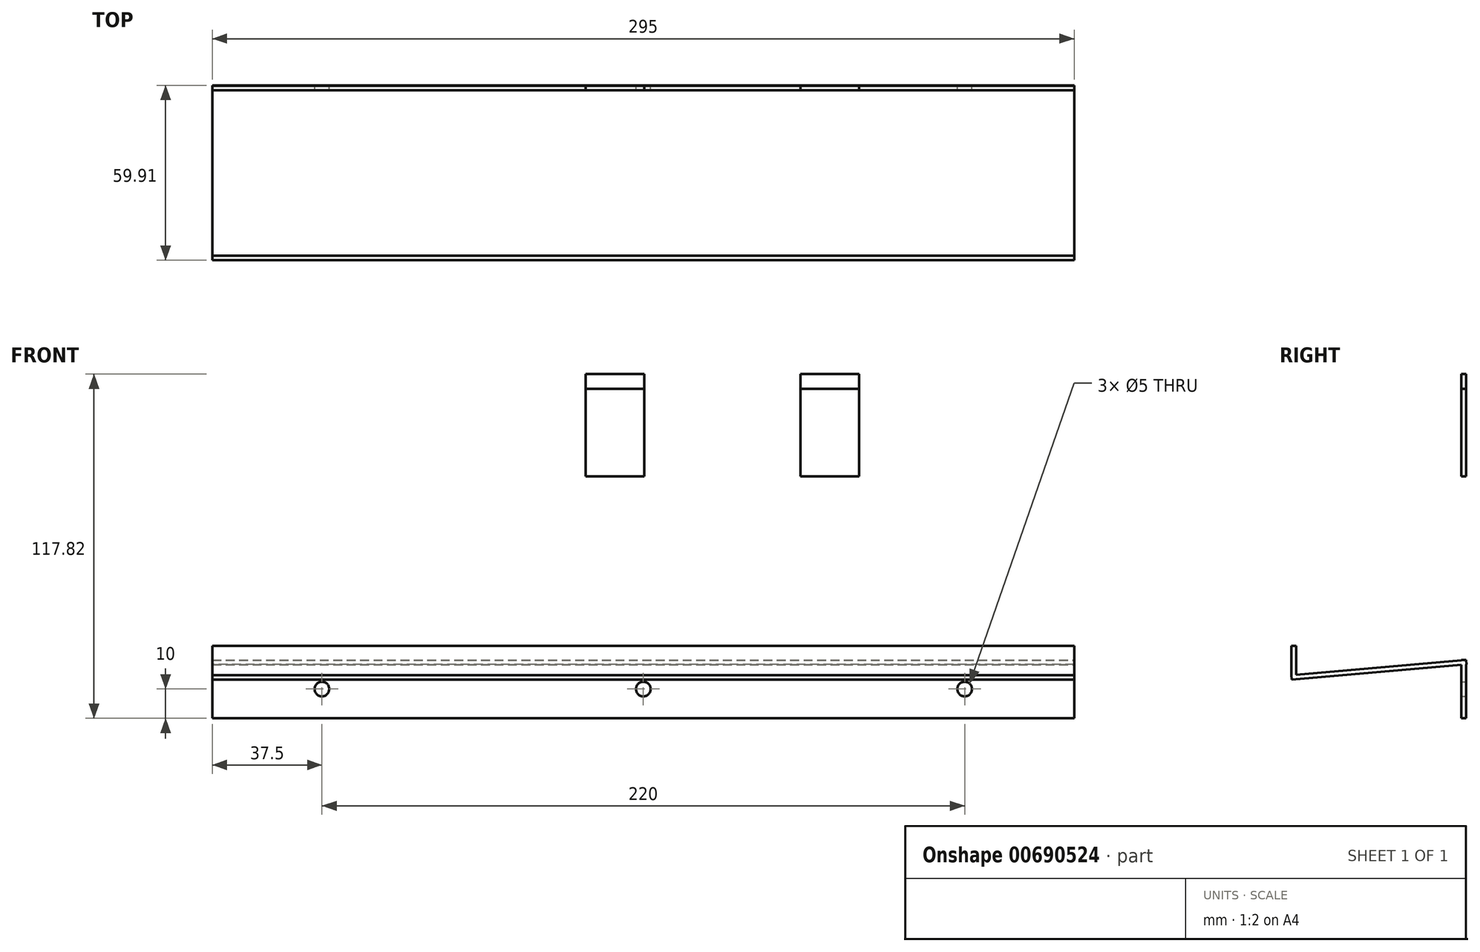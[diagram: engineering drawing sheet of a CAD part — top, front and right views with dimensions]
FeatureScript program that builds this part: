
annotation { "Feature Type Name" : "Feature", "Feature Type Description" : "" }
export const myFeature = defineFeature(function(context is Context, id is Id, definition is map)
    precondition{}
    {
        {
            var Q0;
            Q0=qCreatedBy(makeId("Front.planeOp"),FACE);
            var sketch = newSketch(context, id + "F0", { "sketchPlane" : qUnion([Q0])});
            skLineSegment(sketch, "E0.bottom", {"start": v(0, 0) * mm, "end": v(295, 0) * mm});
            skLineSegment(sketch, "E0.top", {"start": v(0, 20) * mm, "end": v(295, 20) * mm});
            skLineSegment(sketch, "E0.left", {"start": v(0, 0) * mm, "end": v(0, 20) * mm});
            skLineSegment(sketch, "E0.right", {"start": v(295, 0) * mm, "end": v(295, 20) * mm});
            skCircle(sketch, "E1", {"center": v(37.5, 10) * mm, "radius": 2.5 * mm});
            skCircle(sketch, "E2", {"center": v(147.5, 10) * mm, "radius": 2.5 * mm});
            skCircle(sketch, "E3", {"center": v(257.5, 10) * mm, "radius": 2.5 * mm});
            skPoint(sketch, "E4", {"position": v(295, 10) * mm});
            skPoint(sketch, "E5", {"position": v(147.5, 20) * mm});
            skLineSegment(sketch, "E6.bottom", {"start": v(20, 20) * mm, "end": v(275, 20) * mm});
            skLineSegment(sketch, "E6.top", {"start": v(20, 0) * mm, "end": v(275, 0) * mm});
            skLineSegment(sketch, "E6.left", {"start": v(20, 20) * mm, "end": v(20, 0) * mm});
            skLineSegment(sketch, "E6.right", {"start": v(275, 20) * mm, "end": v(275, 0) * mm});
            skSolve(sketch);
        }
        {
            var Q0;
            Q0=sQuery(id+"F0.wireOp",EDGE,"E0.top");
            cPlane(context, id + "F1", {"entities" : qUnion([Q0]), "cplaneType" : CPlaneType.LINE_ANGLE, "offset" : 25 * mm, "angle" : 85 * degree, "oppositeDirection" : true, "width" : 150 * mm, "height" : 150 * mm});
        }
        {
            var Q0;
            Q0=qCreatedBy(id+"F1.planeOp",FACE);
            var sketch = newSketch(context, id + "F2", { "sketchPlane" : qUnion([Q0])});
            skLineSegment(sketch, "E7.bottom", {"start": v(295, -1.74) * mm, "end": v(0, -1.74) * mm});
            skLineSegment(sketch, "E7.top", {"start": v(295, 58.26) * mm, "end": v(0, 58.26) * mm});
            skLineSegment(sketch, "E7.left", {"start": v(295, -1.74) * mm, "end": v(295, 58.26) * mm});
            skLineSegment(sketch, "E7.right", {"start": v(0, -1.74) * mm, "end": v(0, 58.26) * mm});
            skSolve(sketch);
        }
        {
            var Q0;
            Q0=sQuery(id+"F2.wireOp",EDGE,"E7.top");
            cPlane(context, id + "F3", {"entities" : qUnion([Q0]), "cplaneType" : CPlaneType.LINE_ANGLE, "offset" : 25 * mm, "angle" : 0 * degree, "width" : 150 * mm, "height" : 150 * mm});
        }
        {
            var Q0;
            Q0=qCreatedBy(id+"F3.planeOp",FACE);
            var sketch = newSketch(context, id + "F4", { "sketchPlane" : qUnion([Q0])});
            skLineSegment(sketch, "E8.bottom", {"start": v(0, 24.77) * mm, "end": v(295, 24.77) * mm});
            skLineSegment(sketch, "E8.top", {"start": v(0, 14.77) * mm, "end": v(295, 14.77) * mm});
            skLineSegment(sketch, "E8.left", {"start": v(0, 24.77) * mm, "end": v(0, 14.77) * mm});
            skLineSegment(sketch, "E8.right", {"start": v(295, 24.77) * mm, "end": v(295, 14.77) * mm});
            skSolve(sketch);
        }
        {
            var Q0;
            Q0=qCreatedBy(makeId("Front.planeOp"),FACE);
            var sketch = newSketch(context, id + "F5", { "sketchPlane" : qUnion([Q0])});
            skLineSegment(sketch, "E9.bottom", {"start": v(127.8, 117.82) * mm, "end": v(147.8, 117.82) * mm});
            skLineSegment(sketch, "E9.top", {"start": v(127.8, 82.82) * mm, "end": v(147.8, 82.82) * mm});
            skLineSegment(sketch, "E9.left", {"start": v(127.8, 117.82) * mm, "end": v(127.8, 82.82) * mm});
            skLineSegment(sketch, "E9.right", {"start": v(147.8, 117.82) * mm, "end": v(147.8, 82.82) * mm});
            skLineSegment(sketch, "E10", {"start": v(127.8, 112.82) * mm, "end": v(147.8, 112.82) * mm});
            skLineSegment(sketch, "E11", {"start": v(174.57, 135.45) * mm, "end": v(174.57, 78.61) * mm});
            skLineSegment(sketch, "E12.MirrorCS", {"start": v(221.34, 82.82) * mm, "end": v(201.34, 82.82) * mm});
            skLineSegment(sketch, "E13.MirrorCS", {"start": v(221.34, 117.82) * mm, "end": v(221.34, 82.82) * mm});
            skLineSegment(sketch, "E14.MirrorCS", {"start": v(201.34, 117.82) * mm, "end": v(201.34, 82.82) * mm});
            skLineSegment(sketch, "E15.MirrorCS", {"start": v(221.34, 112.82) * mm, "end": v(201.34, 112.82) * mm});
            skLineSegment(sketch, "E16.MirrorCS", {"start": v(221.34, 117.82) * mm, "end": v(201.34, 117.82) * mm});
            skSolve(sketch);
        }
        {
            var Q0;
            {var subQ0=sQuery(id+"F0.wireOp",EDGE,"E0.right");Q0=makeQuery(id+"F0.imprint","IMPRINT",FACE,{"disambiguationData":[TD([[makeQuery(id+"F0.imprint","IMPRINT",EDGE,{"derivedFrom":subQ0}),1.0]])]});}
            var Q1;
            Q1=makeQuery(id+"F0.imprint","IMPRINT",FACE,{"disambiguationData":[TD([[makeQuery(id+"F0.imprint","IMPRINT",EDGE,{"derivedFrom":sQuery(id+"F0.wireOp",EDGE,"E1")}),-1.0]])]});
            var Q2;
            {var subQ0=sQuery(id+"F0.wireOp",EDGE,"E0.left");Q2=makeQuery(id+"F0.imprint","IMPRINT",FACE,{"disambiguationData":[TD([[makeQuery(id+"F0.imprint","IMPRINT",EDGE,{"derivedFrom":subQ0}),-1.0]])]});}
            extrude(context, id + "F6", {"entities" : qUnion([Q0, Q1, Q2]), "depth" : 1.6 * mm, "offsetDistance" : 25 * mm});
        }
        {
            var Q0;
            Q0=makeQuery(id+"F2.imprint","IMPRINT",FACE,{"disambiguationData":[TD([[makeQuery(id+"F2.imprint","IMPRINT",EDGE,{"derivedFrom":sQuery(id+"F2.wireOp",EDGE,"E7.bottom")}),-1.0]])]});
            extrude(context, id + "F7", {"entities" : qUnion([Q0]), "operationType" : NewBodyOperationType.ADD, "depth" : 1.6 * mm, "offsetDistance" : 25 * mm});
        }
        {
            var Q0;
            Q0=makeQuery(id+"F4.imprint","IMPRINT",FACE,{"disambiguationData":[TD([[makeQuery(id+"F4.imprint","IMPRINT",EDGE,{"derivedFrom":sQuery(id+"F4.wireOp",EDGE,"E8.bottom")}),-1.0]])]});
            extrude(context, id + "F8", {"entities" : qUnion([Q0]), "operationType" : NewBodyOperationType.ADD, "oppositeDirection" : true, "depth" : 1.6 * mm, "offsetDistance" : 25 * mm});
        }
        {
            var Q0;
            {var subQ0=sQuery(id+"F5.wireOp",EDGE,"E9.top");Q0=makeQuery(id+"F5.imprint","IMPRINT",FACE,{"disambiguationData":[TD([[makeQuery(id+"F5.imprint","IMPRINT",EDGE,{"derivedFrom":subQ0}),1.0]])]});}
            var Q1;
            {var subQ0=sQuery(id+"F5.wireOp",EDGE,"E12.MirrorCS");Q1=makeQuery(id+"F5.imprint","IMPRINT",FACE,{"disambiguationData":[TD([[makeQuery(id+"F5.imprint","IMPRINT",EDGE,{"derivedFrom":subQ0}),-1.0]])]});}
            extrude(context, id + "F9", {"entities" : qUnion([Q0, Q1]), "depth" : 1.6 * mm, "offsetDistance" : 25 * mm});
        }
        {
            var Q0;
            {var subQ0=sQuery(id+"F5.wireOp",EDGE,"E9.bottom");Q0=makeQuery(id+"F5.imprint","IMPRINT",FACE,{"disambiguationData":[TD([[makeQuery(id+"F5.imprint","IMPRINT",EDGE,{"derivedFrom":subQ0}),-1.0]])]});}
            var Q1;
            {var subQ2=sQuery(id+"F5.wireOp",EDGE,"E15.MirrorCS");Q1=makeQuery(id+"F5.imprint","IMPRINT",FACE,{"disambiguationData":[TD([[makeQuery(id+"F5.imprint","IMPRINT",EDGE,{"derivedFrom":subQ2}),-1.0]])]});}
            extrude(context, id + "F10", {"entities" : qUnion([Q0, Q1]), "depth" : 1.6 * mm, "offsetDistance" : 25 * mm});
        }
    });
